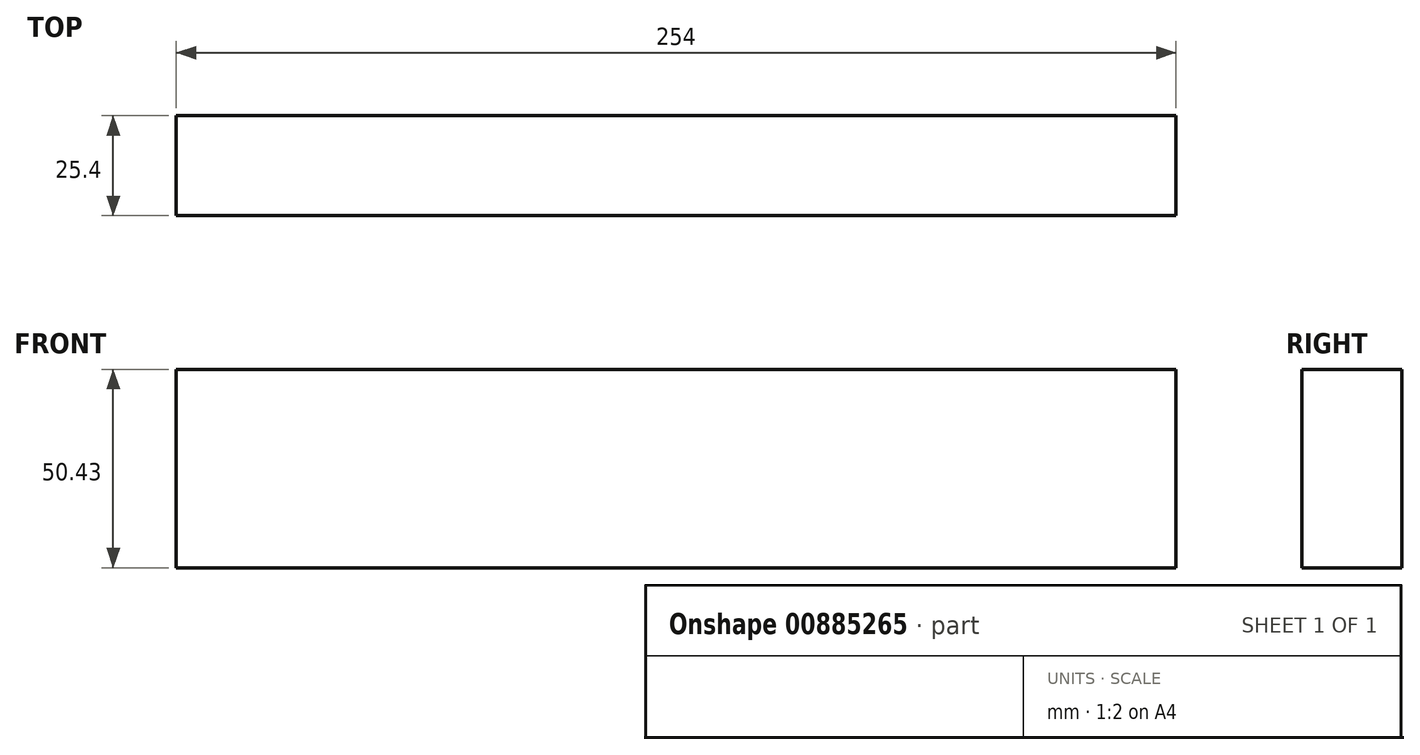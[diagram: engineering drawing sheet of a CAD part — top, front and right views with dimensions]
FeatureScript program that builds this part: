
annotation { "Feature Type Name" : "Feature", "Feature Type Description" : "" }
export const myFeature = defineFeature(function(context is Context, id is Id, definition is map)
    precondition{}
    {
        {
            var Q0;
            Q0=qCreatedBy(makeId("Front.planeOp"),FACE);
            var sketch = newSketch(context, id + "F0", { "sketchPlane" : qUnion([Q0])});
            skLineSegment(sketch, "E0.bottom", {"start": v(-60.1, 0) * mm, "end": v(-20.37, 0) * mm});
            skLineSegment(sketch, "E0.top", {"start": v(-60.1, 50.43) * mm, "end": v(-20.37, 50.43) * mm});
            skLineSegment(sketch, "E0.left", {"start": v(-60.1, 0) * mm, "end": v(-60.1, 50.43) * mm});
            skLineSegment(sketch, "E0.right", {"start": v(-20.37, 0) * mm, "end": v(-20.37, 50.43) * mm});
            skLineSegment(sketch, "E1.bottom", {"start": v(-20.37, 0) * mm, "end": v(27.02, 0) * mm});
            skLineSegment(sketch, "E1.top", {"start": v(-20.37, 50.43) * mm, "end": v(27.02, 50.43) * mm});
            skLineSegment(sketch, "E1.right", {"start": v(27.02, 0) * mm, "end": v(27.02, 50.43) * mm});
            skSolve(sketch);
        }
        {
            var Q0;
            Q0=sQuery(id+"F0.wireOp",EDGE,"E1.right");
            var Q1;
            Q1=sQuery(id+"F0.wireOp",EDGE,"E0.bottom");
            extrude(context, id + "F1", {"bodyType" : ToolBodyType.SURFACE, "surfaceEntities" : qUnion([Q0, Q1]), "depth" : 25.4 * mm, "offsetDistance" : 25.4 * mm});
        }
        {
            var Q0;
            Q0=makeQuery(id+"F1.opExtrude","SWEPT_FACE",FACE,{"disambiguationData":[OSD([sQuery(id+"F0.wireOp",EDGE,"E1.right")])]});
            extrude(context, id + "F2", {"entities" : qUnion([Q0]), "depth" : 254 * mm, "offsetDistance" : 25.4 * mm});
        }
    });
